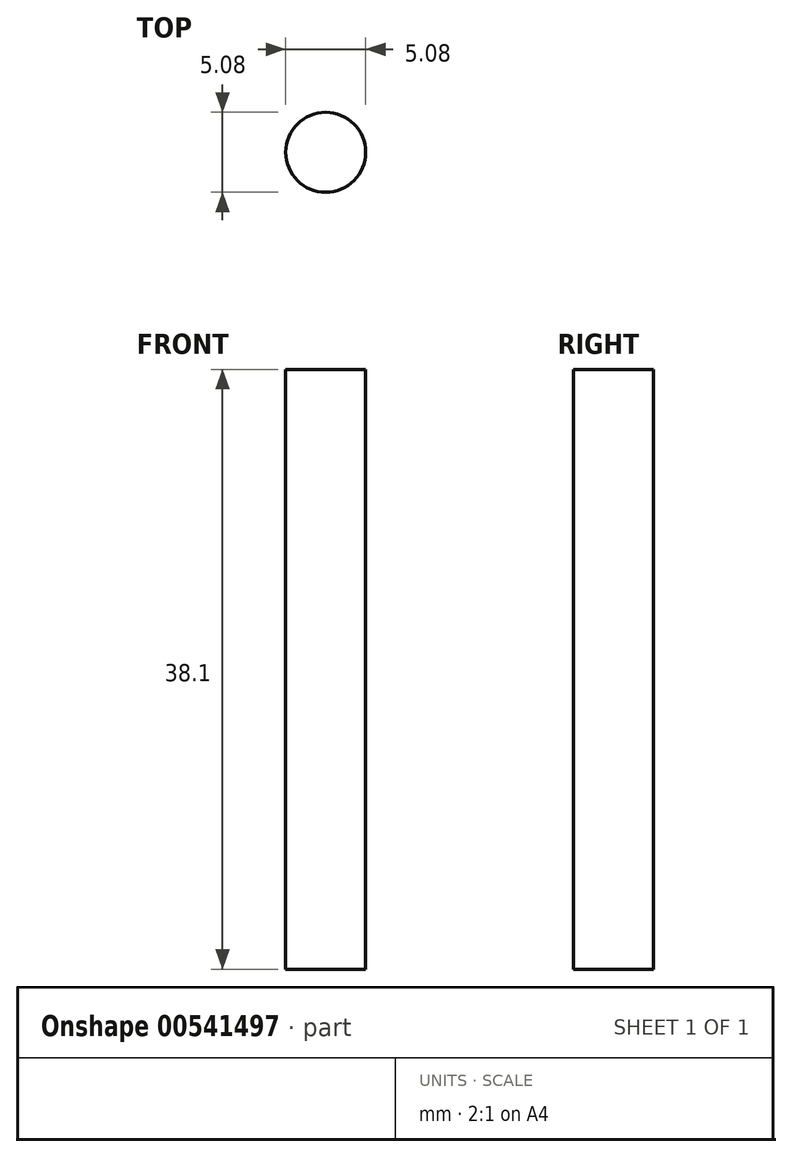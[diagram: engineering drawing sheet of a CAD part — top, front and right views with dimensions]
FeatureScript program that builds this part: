
annotation { "Feature Type Name" : "Feature", "Feature Type Description" : "" }
export const myFeature = defineFeature(function(context is Context, id is Id, definition is map)
    precondition{}
    {
        {
            var Q0;
            Q0=qCreatedBy(makeId("Top.planeOp"),FACE);
            var sketch = newSketch(context, id + "F0", { "sketchPlane" : qUnion([Q0])});
            skCircle(sketch, "E0", {"center": v(-9.53, -15.6) * mm, "radius": 2.54 * mm});
            skSolve(sketch);
        }
        {
            var Q0;
            Q0=makeQuery(id+"F0.imprint","IMPRINT",FACE,{"disambiguationData":[TD([[makeQuery(id+"F0.imprint","IMPRINT",EDGE,{"derivedFrom":sQuery(id+"F0.wireOp",EDGE,"E0")}),1.0]])]});
            extrude(context, id + "F1", {"entities" : qUnion([Q0]), "depth" : 38.1 * mm, "offsetDistance" : 25.4 * mm});
        }
    });
